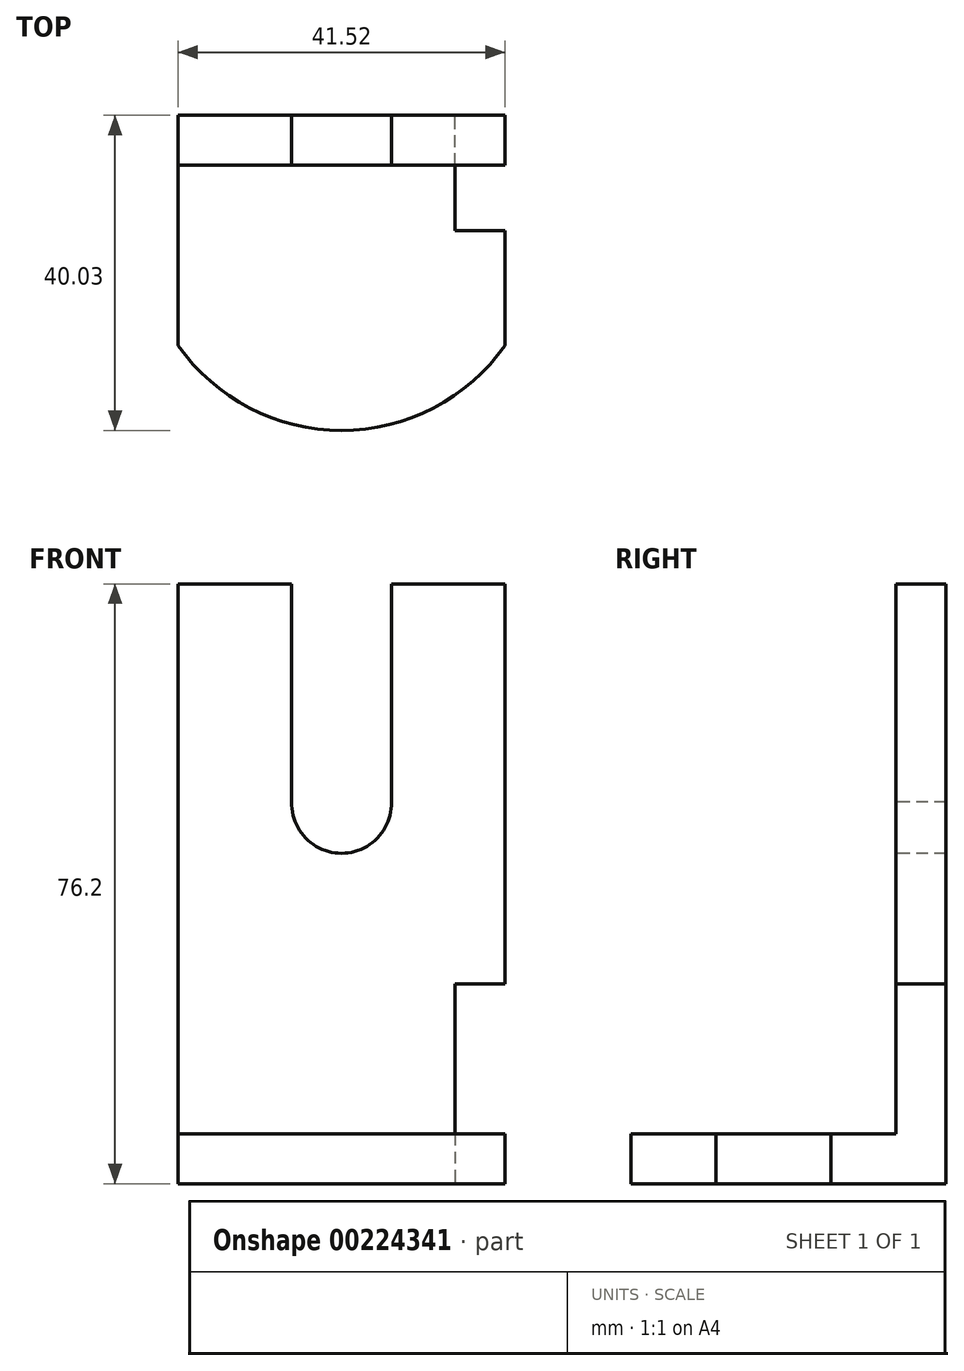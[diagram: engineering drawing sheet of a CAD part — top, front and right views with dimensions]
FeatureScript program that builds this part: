
annotation { "Feature Type Name" : "Feature", "Feature Type Description" : "" }
export const myFeature = defineFeature(function(context is Context, id is Id, definition is map)
    precondition{}
    {
        {
            var Q0;
            Q0=qCreatedBy(makeId("Top.planeOp"),FACE);
            var sketch = newSketch(context, id + "F0", { "sketchPlane" : qUnion([Q0])});
            skCircle(sketch, "E0", {"center": v(0, 0) * mm, "radius": 25.4 * mm});
            skSolve(sketch);
        }
        {
            var Q0;
            Q0=makeQuery(id+"F0.imprint","IMPRINT",FACE,{"disambiguationData":[TD([[makeQuery(id+"F0.imprint","IMPRINT",EDGE,{"derivedFrom":sQuery(id+"F0.wireOp",EDGE,"E0")}),1.0]])]});
            extrude(context, id + "F1", {"entities" : qUnion([Q0]), "depth" : 76.2 * mm});
        }
        {
            var Q0;
            Q0=makeQuery(id+"F1.opExtrude","CAP_FACE",FACE,{"disambiguationData":[OSD([sQuery(id+"F0.wireOp",EDGE,"E0")])],"isStart":false});
            var sketch = newSketch(context, id + "F2", { "sketchPlane" : qUnion([Q0])});
            skLineSegment(sketch, "E1.left", {"start": v(-20.76, 19.49) * mm, "end": v(-20.76, -19.49) * mm});
            skLineSegment(sketch, "E1.right", {"start": v(20.76, 19.49) * mm, "end": v(20.76, -19.49) * mm});
            skPoint(sketch, "E1.middle", {"position": v(0, 0) * mm});
            skLineSegment(sketch, "E2", {"start": v(-20.76, 14.63) * mm, "end": v(20.76, 14.63) * mm});
            skSolve(sketch);
        }
        {
            var Q0;
            {var subQ0=sQuery(id+"F2.wireOp",EDGE,"E1.right");var subQ1=makeQuery(id+"F1.opExtrude","CAP_EDGE",EDGE,{"disambiguationData":[OSD([sQuery(id+"F0.wireOp",EDGE,"E0")])],"isStart":false});var subQ2=makeQuery(id+"F2.imprint","INTERSECT",VERTEX,{"disambiguationData":[OD(0.0)],"derivedFrom":[subQ1,subQ0]});Q0=makeQuery(id+"F2.imprint","IMPRINT",FACE,{"disambiguationData":[TD([[makeQuery(id+"F2.imprint","IMPRINT",EDGE,{"disambiguationData":[TD([[subQ2,1.0]])],"derivedFrom":subQ0}),1.0]])]});}
            var Q1;
            {var subQ0=sQuery(id+"F2.wireOp",EDGE,"E1.left");var subQ1=makeQuery(id+"F1.opExtrude","CAP_EDGE",EDGE,{"disambiguationData":[OSD([sQuery(id+"F0.wireOp",EDGE,"E0")])],"isStart":false});var subQ2=makeQuery(id+"F2.imprint","INTERSECT",VERTEX,{"disambiguationData":[OD(0.0)],"derivedFrom":[subQ1,subQ0]});Q1=makeQuery(id+"F2.imprint","IMPRINT",FACE,{"disambiguationData":[TD([[makeQuery(id+"F2.imprint","IMPRINT",EDGE,{"disambiguationData":[TD([[subQ2,1.0]])],"derivedFrom":subQ0}),-1.0]])]});}
            var Q2;
            {var subQ0=sQuery(id+"F2.wireOp",EDGE,"E2");Q2=makeQuery(id+"F2.imprint","IMPRINT",FACE,{"disambiguationData":[TD([[makeQuery(id+"F2.imprint","IMPRINT",EDGE,{"derivedFrom":subQ0}),1.0]])]});}
            extrude(context, id + "F3", {"entities" : qUnion([Q0, Q1, Q2]), "operationType" : NewBodyOperationType.REMOVE, "oppositeDirection" : true, "depth" : 99.31 * mm});
        }
        {
            var Q0;
            Q0=makeQuery(id+"F1.opExtrude","CAP_FACE",FACE,{"disambiguationData":[OSD([sQuery(id+"F0.wireOp",EDGE,"E0")])],"isStart":true});
            var sketch = newSketch(context, id + "F4", { "sketchPlane" : qUnion([Q0])});
            skLineSegment(sketch, "E3.bottom", {"start": v(20.76, 0) * mm, "end": v(14.41, 0) * mm});
            skLineSegment(sketch, "E3.top", {"start": v(20.76, -24.19) * mm, "end": v(14.41, -24.19) * mm});
            skLineSegment(sketch, "E3.left", {"start": v(20.76, 0) * mm, "end": v(20.76, -24.19) * mm});
            skLineSegment(sketch, "E3.right", {"start": v(14.41, 0) * mm, "end": v(14.41, -24.19) * mm});
            skSolve(sketch);
        }
        {
            var Q0;
            Q0 = qSketchRegion(id + "F4", true);
            extrude(context, id + "F5", {"entities" : qUnion([Q0]), "operationType" : NewBodyOperationType.REMOVE, "oppositeDirection" : true, "depth" : 25.4 * mm});
        }
        {
            var Q0;
            Q0=makeQuery(id+"F3.boolean.opBoolean","COPY",FACE,{"derivedFrom":makeQuery(id+"F3.opExtrude","SWEPT_FACE",FACE,{"disambiguationData":[OSD([sQuery(id+"F2.wireOp",EDGE,"E1.left")])]})});
            var sketch = newSketch(context, id + "F6", { "sketchPlane" : qUnion([Q0])});
            skLineSegment(sketch, "E4.bottom", {"start": v(-8.28, 76.2) * mm, "end": v(42.52, 76.2) * mm});
            skLineSegment(sketch, "E4.top", {"start": v(-8.28, 6.35) * mm, "end": v(42.52, 6.35) * mm});
            skLineSegment(sketch, "E4.left", {"start": v(-8.28, 76.2) * mm, "end": v(-8.28, 6.35) * mm});
            skLineSegment(sketch, "E4.right", {"start": v(42.52, 76.2) * mm, "end": v(42.52, 6.35) * mm});
            skSolve(sketch);
        }
        {
            var Q0;
            Q0 = qSketchRegion(id + "F6", true);
            extrude(context, id + "F7", {"entities" : qUnion([Q0]), "operationType" : NewBodyOperationType.REMOVE, "oppositeDirection" : true, "depth" : 123.95 * mm});
        }
        {
            var Q0;
            Q0=makeQuery(id+"F7.boolean.opBoolean","COPY",FACE,{"derivedFrom":makeQuery(id+"F7.opExtrude","SWEPT_FACE",FACE,{"disambiguationData":[OSD([sQuery(id+"F6.wireOp",EDGE,"E4.left")])]})});
            var sketch = newSketch(context, id + "F8", { "sketchPlane" : qUnion([Q0])});
            skCircle(sketch, "E5", {"center": v(0, 48.32) * mm, "radius": 6.35 * mm});
            skLineSegment(sketch, "E6", {"start": v(-6.35, 48.49) * mm, "end": v(-6.35, 76.2) * mm});
            skLineSegment(sketch, "E7", {"start": v(6.35, 48.48) * mm, "end": v(6.35, 76.2) * mm});
            skSolve(sketch);
        }
        {
            var Q0;
            {var subQ0=sQuery(id+"F8.wireOp",EDGE,"E6");Q0=makeQuery(id+"F8.imprint","IMPRINT",FACE,{"disambiguationData":[TD([[makeQuery(id+"F8.imprint","IMPRINT",EDGE,{"derivedFrom":subQ0}),-1.0]])]});}
            var Q1;
            {var subQ0=sQuery(id+"F8.wireOp",EDGE,"E5");var subQ1=makeQuery(id+"F8.imprint","INTERSECT",VERTEX,{"derivedFrom":[subQ0,sQuery(id+"F8.wireOp",EDGE,"E6")]});Q1=makeQuery(id+"F8.imprint","IMPRINT",FACE,{"disambiguationData":[TD([[makeQuery(id+"F8.imprint","IMPRINT",EDGE,{"disambiguationData":[TD([[subQ1,1.0]])],"derivedFrom":subQ0}),1.0]])]});}
            extrude(context, id + "F9", {"entities" : qUnion([Q0, Q1]), "operationType" : NewBodyOperationType.REMOVE, "oppositeDirection" : true, "depth" : 25.4 * mm});
        }
    });
